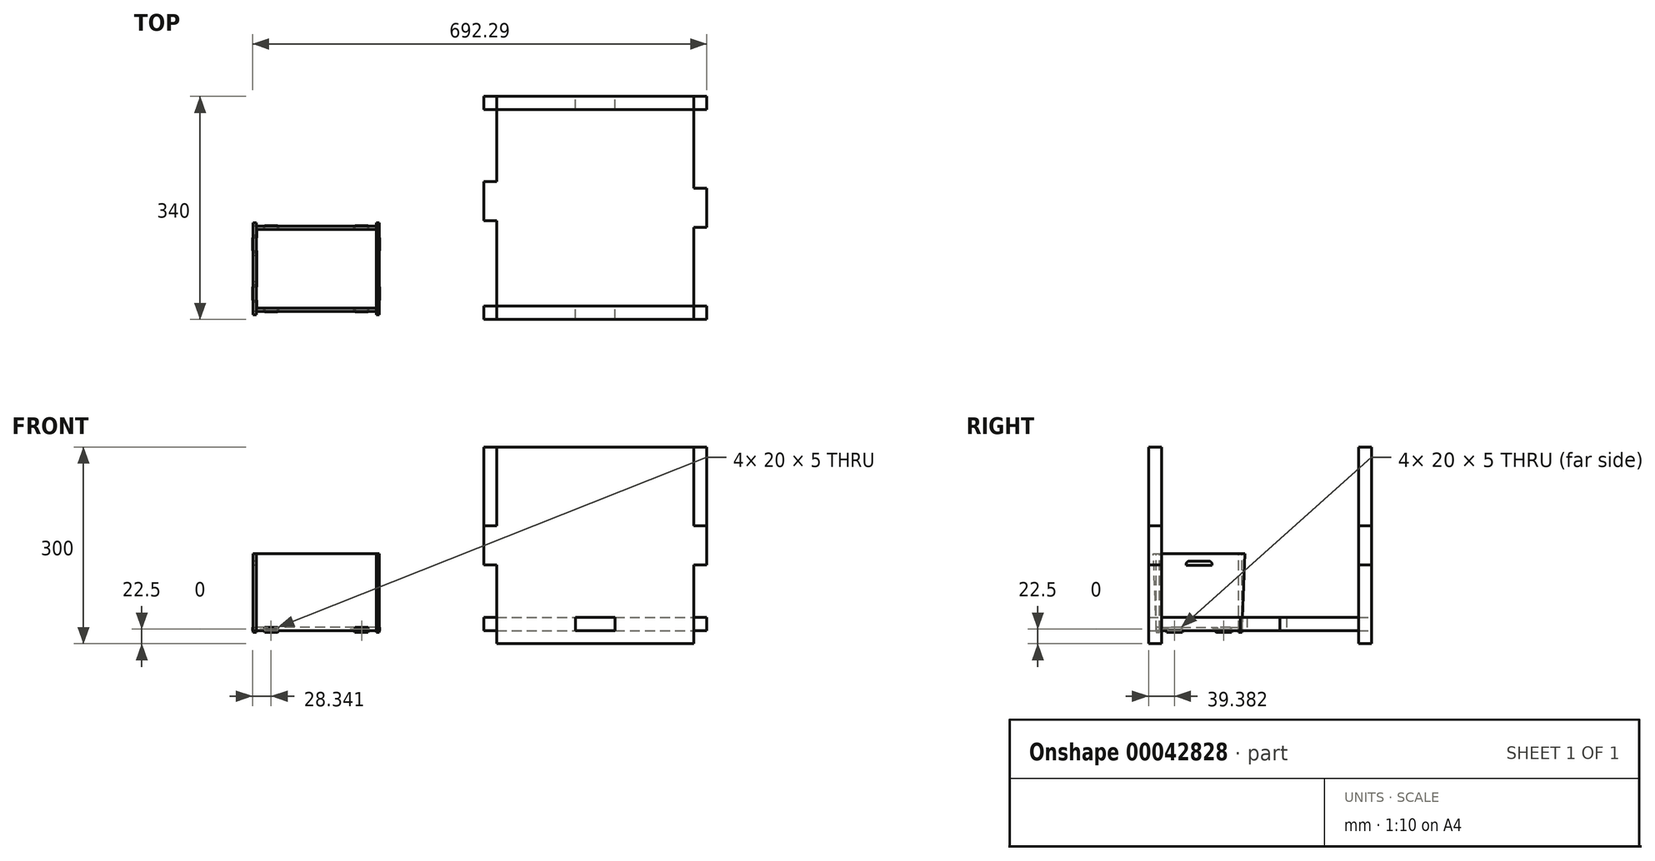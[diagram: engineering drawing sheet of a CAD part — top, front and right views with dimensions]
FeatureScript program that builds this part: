
annotation { "Feature Type Name" : "Feature", "Feature Type Description" : "" }
export const myFeature = defineFeature(function(context is Context, id is Id, definition is map)
    precondition{}
    {
        {
            var Q0;
            Q0=qCreatedBy(makeId("Top.planeOp"),FACE);
            var sketch = newSketch(context, id + "F0", { "sketchPlane" : qUnion([Q0])});
            skLineSegment(sketch, "E0.rect.bottom", {"start": v(91.08, -60.14) * mm, "end": v(-91.08, -60.14) * mm});
            skLineSegment(sketch, "E0.rect.top", {"start": v(91.08, 60.14) * mm, "end": v(-91.08, 60.14) * mm});
            skLineSegment(sketch, "E0.rect.left", {"start": v(91.08, -60.14) * mm, "end": v(91.08, 60.14) * mm});
            skLineSegment(sketch, "E0.rect.right", {"start": v(-91.08, -60.14) * mm, "end": v(-91.08, 60.14) * mm});
            skPoint(sketch, "E0.rect.middle", {"position": v(0, 0) * mm});
            skLineSegment(sketch, "E1.rect.bottom", {"start": v(78.98, 54.64) * mm, "end": v(58.98, 54.64) * mm});
            skLineSegment(sketch, "E1.rect.top", {"start": v(78.98, 65.64) * mm, "end": v(58.98, 65.64) * mm});
            skLineSegment(sketch, "E1.rect.left", {"start": v(78.98, 54.64) * mm, "end": v(78.98, 65.64) * mm});
            skLineSegment(sketch, "E1.rect.right", {"start": v(58.98, 54.64) * mm, "end": v(58.98, 65.64) * mm});
            skPoint(sketch, "E1.rect.middle", {"position": v(68.98, 60.14) * mm});
            skLineSegment(sketch, "E2.rect.bottom", {"start": v(58.98, -54.64) * mm, "end": v(78.98, -54.64) * mm});
            skLineSegment(sketch, "E2.rect.top", {"start": v(58.98, -65.64) * mm, "end": v(78.98, -65.64) * mm});
            skLineSegment(sketch, "E2.rect.left", {"start": v(58.98, -54.64) * mm, "end": v(58.98, -65.64) * mm});
            skLineSegment(sketch, "E2.rect.right", {"start": v(78.98, -54.64) * mm, "end": v(78.98, -65.64) * mm});
            skPoint(sketch, "E2.rect.middle", {"position": v(68.98, -60.14) * mm});
            skLineSegment(sketch, "E3.rect.bottom", {"start": v(96.58, 27.63) * mm, "end": v(85.58, 27.63) * mm});
            skLineSegment(sketch, "E3.rect.top", {"start": v(96.58, 47.63) * mm, "end": v(85.58, 47.63) * mm});
            skLineSegment(sketch, "E3.rect.left", {"start": v(96.58, 27.63) * mm, "end": v(96.58, 47.63) * mm});
            skLineSegment(sketch, "E3.rect.right", {"start": v(85.58, 27.63) * mm, "end": v(85.58, 47.63) * mm});
            skPoint(sketch, "E3.rect.middle", {"position": v(91.08, 37.63) * mm});
            skLineSegment(sketch, "E4.rect.bottom", {"start": v(-97.32, 47.63) * mm, "end": v(-86.32, 47.63) * mm});
            skLineSegment(sketch, "E4.rect.top", {"start": v(-97.32, 27.63) * mm, "end": v(-86.32, 27.63) * mm});
            skLineSegment(sketch, "E4.rect.left", {"start": v(-97.32, 47.63) * mm, "end": v(-97.32, 27.63) * mm});
            skLineSegment(sketch, "E4.rect.right", {"start": v(-86.32, 47.63) * mm, "end": v(-86.32, 27.63) * mm});
            skLineSegment(sketch, "E5", {"start": v(0, -60.14) * mm, "end": v(0, -76.16) * mm, "construction": true});
            skLineSegment(sketch, "E6.MirrorCS", {"start": v(-58.98, -65.64) * mm, "end": v(-78.98, -65.64) * mm});
            skLineSegment(sketch, "E7.MirrorCS", {"start": v(-58.98, -54.64) * mm, "end": v(-58.98, -65.64) * mm});
            skLineSegment(sketch, "E8.MirrorCS", {"start": v(-78.98, -54.64) * mm, "end": v(-78.98, -65.64) * mm});
            skPoint(sketch, "E9", {"position": v(-91.08, 0) * mm});
            skLineSegment(sketch, "E10", {"start": v(-91.08, 0) * mm, "end": v(-66.47, 0) * mm, "construction": true});
            skLineSegment(sketch, "E11.MirrorCS", {"start": v(-97.32, -27.63) * mm, "end": v(-86.32, -27.63) * mm});
            skLineSegment(sketch, "E12.MirrorCS", {"start": v(-97.32, -47.63) * mm, "end": v(-97.32, -27.63) * mm});
            skLineSegment(sketch, "E13.MirrorCS", {"start": v(-97.32, -47.63) * mm, "end": v(-86.32, -47.63) * mm});
            skLineSegment(sketch, "E14.MirrorCS", {"start": v(96.58, -27.63) * mm, "end": v(85.58, -27.63) * mm});
            skLineSegment(sketch, "E15.MirrorCS", {"start": v(96.58, -27.63) * mm, "end": v(96.58, -47.63) * mm});
            skLineSegment(sketch, "E16.MirrorCS", {"start": v(96.58, -47.63) * mm, "end": v(85.58, -47.63) * mm});
            skLineSegment(sketch, "E17.bottom", {"start": v(-78.98, 53.09) * mm, "end": v(-58.98, 53.09) * mm});
            skLineSegment(sketch, "E17.top", {"start": v(-78.98, 65.64) * mm, "end": v(-58.98, 65.64) * mm});
            skLineSegment(sketch, "E17.left", {"start": v(-78.98, 53.09) * mm, "end": v(-78.98, 65.64) * mm});
            skLineSegment(sketch, "E17.right", {"start": v(-58.98, 53.09) * mm, "end": v(-58.98, 65.64) * mm});
            skSolve(sketch);
        }
        {
            var Q0;
            Q0 = qSketchRegion(id + "F0", true);
            extrude(context, id + "F1", {"entities" : qUnion([Q0]), "depth" : 5 * mm});
        }
        {
            var Q0;
            {var subQ0=sQuery(id+"F0.wireOp",EDGE,"E0.rect.left");Q0=makeQuery(id+"F1.opExtrude","SWEPT_FACE",FACE,{"disambiguationData":[OSD([subQ0]),TDD([makeQuery(id+"F0.imprint","IMPRINT",EDGE,{"disambiguationData":[TD([[makeQuery(id+"F0.imprint","INTERSECT",VERTEX,{"derivedFrom":[sQuery(id+"F0.wireOp",EDGE,"E0.rect.bottom"),subQ0]}),-1.0]])],"derivedFrom":subQ0})])]});}
            var sketch = newSketch(context, id + "F2", { "sketchPlane" : qUnion([Q0])});
            skLineSegment(sketch, "E18.bottom", {"start": v(-65, -2.63) * mm, "end": v(-25.7, -2.63) * mm});
            skLineSegment(sketch, "E18.top", {"start": v(-65, 117.37) * mm, "end": v(65, 117.37) * mm});
            skLineSegment(sketch, "E18.left", {"start": v(-65, -2.63) * mm, "end": v(-65, 117.37) * mm});
            skLineSegment(sketch, "E18.right", {"start": v(65, -2.63) * mm, "end": v(65, 117.37) * mm});
            skLineSegment(sketch, "E19", {"start": v(-65, -2.63) * mm, "end": v(-70, 117.37) * mm});
            skLineSegment(sketch, "E20", {"start": v(-70, 117.37) * mm, "end": v(-65, 117.37) * mm});
            skLineSegment(sketch, "E21", {"start": v(65, 117.37) * mm, "end": v(70, 117.37) * mm});
            skLineSegment(sketch, "E22", {"start": v(70, 117.37) * mm, "end": v(65, -2.63) * mm});
            skPoint(sketch, "E23", {"position": v(0, -2.63) * mm});
            skLineSegment(sketch, "E24", {"start": v(-50.88, 0) * mm, "end": v(-65.1, 0) * mm});
            skLineSegment(sketch, "E25", {"start": v(0, -2.63) * mm, "end": v(0, -7.24) * mm, "construction": true});
            skLineSegment(sketch, "E26.MirrorCS", {"start": v(50.88, 0) * mm, "end": v(65.1, 0) * mm});
            skLineSegment(sketch, "E27", {"start": v(-50.88, 0) * mm, "end": v(-49.45, -2.63) * mm});
            skLineSegment(sketch, "E28", {"start": v(-24.16, 0) * mm, "end": v(-25.7, -2.63) * mm});
            skLineSegment(sketch, "E29.MirrorCS", {"start": v(24.16, 0) * mm, "end": v(25.7, -2.63) * mm});
            skLineSegment(sketch, "E30.MirrorCS", {"start": v(50.88, 0) * mm, "end": v(49.45, -2.63) * mm});
            skLineSegment(sketch, "E31.trimOffspring", {"start": v(25.7, -2.63) * mm, "end": v(65, -2.63) * mm});
            skLineSegment(sketch, "E32", {"start": v(-24.16, 0) * mm, "end": v(24.16, 0) * mm});
            skSolve(sketch);
        }
        {
            var Q0;
            {var subQ0=sQuery(id+"F0.wireOp",EDGE,"E0.rect.left");var subQ1=sQuery(id+"F0.wireOp",EDGE,"E3.rect.bottom");Q0=makeQuery(id+"F2.imprint","IMPRINT",FACE,{"disambiguationData":[TD([[makeQuery(id+"F2.imprint","IMPRINT",EDGE,{"derivedFrom":makeQuery(id+"F1.opExtrude","SWEPT_EDGE",EDGE,{"disambiguationData":[OSD([subQ0,subQ1])]})}),-1.0]])]});}
            var Q1;
            {var subQ1=sQuery(id+"F0.wireOp",EDGE,"E0.rect.left");var subQ3=sQuery(id+"F0.wireOp",EDGE,"E0.rect.bottom");var subQ7=makeQuery(id+"F1.opExtrude","SWEPT_EDGE",EDGE,{"disambiguationData":[OSD([subQ3,subQ1])]});Q1=makeQuery(id+"F2.imprint","IMPRINT",FACE,{"disambiguationData":[TD([[makeQuery(id+"F2.imprint","IMPRINT",EDGE,{"derivedFrom":subQ7}),1.0]])]});}
            var Q2;
            {var subQ8=sQuery(id+"F2.wireOp",EDGE,"E18.top");Q2=makeQuery(id+"F2.imprint","IMPRINT",FACE,{"disambiguationData":[TD([[makeQuery(id+"F2.imprint","IMPRINT",EDGE,{"derivedFrom":subQ8}),-1.0]])]});}
            var Q3;
            {var subQ0=sQuery(id+"F2.wireOp",EDGE,"E20");Q3=makeQuery(id+"F2.imprint","IMPRINT",FACE,{"disambiguationData":[TD([[makeQuery(id+"F2.imprint","IMPRINT",EDGE,{"derivedFrom":subQ0}),-1.0]])]});}
            var Q4;
            {var subQ5=sQuery(id+"F2.wireOp",EDGE,"E21");Q4=makeQuery(id+"F2.imprint","IMPRINT",FACE,{"disambiguationData":[TD([[makeQuery(id+"F2.imprint","IMPRINT",EDGE,{"derivedFrom":subQ5}),-1.0]])]});}
            extrude(context, id + "F3", {"entities" : qUnion([Q0, Q1, Q2, Q3, Q4]), "depth" : 5 * mm});
        }
        {
            var Q0;
            Q0=makeQuery(id+"F3.opExtrude","SWEPT_BODY",BODY,{"disambiguationData":[OSD([sQuery(id+"F2.wireOp",EDGE,"E18.bottom"),sQuery(id+"F2.wireOp",EDGE,"E18.top"),sQuery(id+"F2.wireOp",EDGE,"E19"),sQuery(id+"F2.wireOp",EDGE,"E20"),sQuery(id+"F2.wireOp",EDGE,"E21"),sQuery(id+"F2.wireOp",EDGE,"E22")])]});
            var Q1;
            {var subQ0=sQuery(id+"F0.wireOp",EDGE,"E0.rect.bottom");Q1=makeQuery(id+"F1.opExtrude","CAP_EDGE",EDGE,{"disambiguationData":[OSD([subQ0]),TDD([makeQuery(id+"F0.imprint","IMPRINT",EDGE,{"disambiguationData":[TD([[makeQuery(id+"F0.imprint","INTERSECT",VERTEX,{"derivedFrom":[subQ0,sQuery(id+"F0.wireOp",EDGE,"E7.MirrorCS")]}),1.0]])],"derivedFrom":subQ0})])],"isStart":false});}
            transform(context, id + "F4", {"entities" : qUnion([Q0]), "transformType" : TransformType.TRANSLATION_DISTANCE, "transformDirection" : qUnion([Q1]), "distance" : 187.5 * mm, "makeCopy" : true});
        }
        {
            var Q0;
            {var subQ0=sQuery(id+"F0.wireOp",EDGE,"E0.rect.bottom");Q0=makeQuery(id+"F1.opExtrude","SWEPT_FACE",FACE,{"disambiguationData":[OSD([subQ0]),TDD([makeQuery(id+"F0.imprint","IMPRINT",EDGE,{"disambiguationData":[TD([[makeQuery(id+"F0.imprint","INTERSECT",VERTEX,{"derivedFrom":[subQ0,sQuery(id+"F0.wireOp",EDGE,"E0.rect.right")]}),1.0]])],"derivedFrom":subQ0})])]});}
            var sketch = newSketch(context, id + "F5", { "sketchPlane" : qUnion([Q0])});
            skLineSegment(sketch, "E33.bottom", {"start": v(-91.42, -2.63) * mm, "end": v(91.08, -2.63) * mm});
            skLineSegment(sketch, "E33.top", {"start": v(-91.42, 117.37) * mm, "end": v(91.08, 117.37) * mm});
            skLineSegment(sketch, "E33.left", {"start": v(-91.42, -2.63) * mm, "end": v(-91.42, 117.37) * mm});
            skLineSegment(sketch, "E33.right", {"start": v(91.08, -2.63) * mm, "end": v(91.08, 117.37) * mm});
            skLineSegment(sketch, "E34", {"start": v(-91.42, 0) * mm, "end": v(-80.28, 0) * mm});
            skLineSegment(sketch, "E35", {"start": v(-80.28, 0) * mm, "end": v(-79.07, -2.63) * mm});
            skLineSegment(sketch, "E36", {"start": v(-57.5, 0) * mm, "end": v(-58.88, -2.63) * mm});
            skLineSegment(sketch, "E37", {"start": v(-0.17, -5.62) * mm, "end": v(-0.17, -18.88) * mm, "construction": true});
            skPoint(sketch, "E37.startSnap0", {"position": v(-0.17, -2.63) * mm});
            skLineSegment(sketch, "E38.MirrorCS", {"start": v(57.17, 0) * mm, "end": v(58.54, -2.63) * mm});
            skLineSegment(sketch, "E39.MirrorCS", {"start": v(79.94, 0) * mm, "end": v(78.74, -2.63) * mm});
            skLineSegment(sketch, "E40.MirrorCS", {"start": v(91.08, 0) * mm, "end": v(79.94, 0) * mm});
            skLineSegment(sketch, "E41", {"start": v(-57.5, 0) * mm, "end": v(57.17, 0) * mm});
            skSolve(sketch);
        }
        {
            var Q0;
            {var subQ3=sQuery(id+"F5.wireOp",EDGE,"E33.bottom");Q0=makeQuery(id+"F5.imprint","IMPRINT",FACE,{"disambiguationData":[TD([[makeQuery(id+"F5.imprint","IMPRINT",EDGE,{"derivedFrom":subQ3}),1.0]])]});}
            var Q1;
            {var subQ0=sQuery(id+"F0.wireOp",EDGE,"E0.rect.bottom");var subQ2=sQuery(id+"F0.wireOp",EDGE,"E0.rect.right");Q1=makeQuery(id+"F5.imprint","IMPRINT",FACE,{"disambiguationData":[TD([[makeQuery(id+"F5.imprint","IMPRINT",EDGE,{"derivedFrom":makeQuery(id+"F1.opExtrude","SWEPT_EDGE",EDGE,{"disambiguationData":[OSD([subQ0,subQ2])]})}),1.0]])]});}
            extrude(context, id + "F6", {"entities" : qUnion([Q0, Q1]), "depth" : 5 * mm});
        }
        {
            var Q0;
            Q0=makeQuery(id+"F6.opExtrude","SWEPT_BODY",BODY,{"disambiguationData":[OSD([sQuery(id+"F5.wireOp",EDGE,"E33.bottom"),sQuery(id+"F5.wireOp",EDGE,"E33.top"),sQuery(id+"F5.wireOp",EDGE,"E33.left"),sQuery(id+"F5.wireOp",EDGE,"E33.right"),sQuery(id+"F5.wireOp",EDGE,"E34"),sQuery(id+"F5.wireOp",EDGE,"E35"),sQuery(id+"F5.wireOp",EDGE,"E36"),sQuery(id+"F5.wireOp",EDGE,"E38.MirrorCS"),sQuery(id+"F5.wireOp",EDGE,"E39.MirrorCS"),sQuery(id+"F5.wireOp",EDGE,"E40.MirrorCS"),sQuery(id+"F5.wireOp",EDGE,"E41")])]});
            var Q1;
            {var subQ0=sQuery(id+"F0.wireOp",EDGE,"E0.rect.left");Q1=makeQuery(id+"F1.opExtrude","CAP_EDGE",EDGE,{"disambiguationData":[OSD([subQ0]),TDD([makeQuery(id+"F0.imprint","IMPRINT",EDGE,{"disambiguationData":[TD([[makeQuery(id+"F0.imprint","INTERSECT",VERTEX,{"derivedFrom":[sQuery(id+"F0.wireOp",EDGE,"E0.rect.bottom"),subQ0]}),-1.0]])],"derivedFrom":subQ0})])],"isStart":false});}
            var Q2;
            Q2=makeQuery(id+"F1.opExtrude","CAP_EDGE",EDGE,{"disambiguationData":[OSD([sQuery(id+"F0.wireOp",EDGE,"E3.rect.left")])],"isStart":false});
            var Q3;
            Q3=makeQuery(id+"F4.opPattern","COPY",EDGE,{"derivedFrom":makeQuery(id+"F3.opExtrude","CAP_EDGE",EDGE,{"disambiguationData":[OSD([sQuery(id+"F2.wireOp",EDGE,"E18.top")])],"isStart":false}),"instanceName":"1"});
            transform(context, id + "F7", {"entities" : qUnion([Q0]), "transformType" : TransformType.TRANSLATION_DISTANCE, "transformDirection" : qUnion([Q3]), "distance" : 125.5 * mm, "makeCopy" : true});
        }
        {
            var Q0;
            Q0=makeQuery(id+"F1.opExtrude","SWEPT_BODY",BODY,{"disambiguationData":[OSD([sQuery(id+"F0.wireOp",EDGE,"E0.rect.bottom"),sQuery(id+"F0.wireOp",EDGE,"E0.rect.top"),sQuery(id+"F0.wireOp",EDGE,"E0.rect.left"),sQuery(id+"F0.wireOp",EDGE,"E0.rect.right"),sQuery(id+"F0.wireOp",EDGE,"E1.rect.top"),sQuery(id+"F0.wireOp",EDGE,"E1.rect.left"),sQuery(id+"F0.wireOp",EDGE,"E1.rect.right"),sQuery(id+"F0.wireOp",EDGE,"E2.rect.top"),sQuery(id+"F0.wireOp",EDGE,"E2.rect.left"),sQuery(id+"F0.wireOp",EDGE,"E2.rect.right"),sQuery(id+"F0.wireOp",EDGE,"E3.rect.bottom"),sQuery(id+"F0.wireOp",EDGE,"E3.rect.top"),sQuery(id+"F0.wireOp",EDGE,"E3.rect.left"),sQuery(id+"F0.wireOp",EDGE,"E4.rect.bottom"),sQuery(id+"F0.wireOp",EDGE,"E4.rect.top"),sQuery(id+"F0.wireOp",EDGE,"E4.rect.left")])]});
            var Q1;
            Q1=makeQuery(id+"F7.opPattern","COPY",BODY,{"derivedFrom":makeQuery(id+"F6.opExtrude","SWEPT_BODY",BODY,{"disambiguationData":[OSD([sQuery(id+"F5.wireOp",EDGE,"46b3cb84-1207-44b6-bca0-a6f87da00f9c.bottom"),sQuery(id+"F5.wireOp",EDGE,"46b3cb84-1207-44b6-bca0-a6f87da00f9c.top"),sQuery(id+"F5.wireOp",EDGE,"46b3cb84-1207-44b6-bca0-a6f87da00f9c.left"),sQuery(id+"F5.wireOp",EDGE,"46b3cb84-1207-44b6-bca0-a6f87da00f9c.right"),sQuery(id+"F5.wireOp",EDGE,"da92aac8-b902-4d4c-b7ad-71e9202061bc.rect.bottom"),sQuery(id+"F5.wireOp",EDGE,"da92aac8-b902-4d4c-b7ad-71e9202061bc.rect.top"),sQuery(id+"F5.wireOp",EDGE,"da92aac8-b902-4d4c-b7ad-71e9202061bc.rect.left"),sQuery(id+"F5.wireOp",EDGE,"ea491399-d061-4eb9-b57f-cc231cf8a471.rect.bottom"),sQuery(id+"F5.wireOp",EDGE,"ea491399-d061-4eb9-b57f-cc231cf8a471.rect.top"),sQuery(id+"F5.wireOp",EDGE,"ea491399-d061-4eb9-b57f-cc231cf8a471.rect.right")])]}),"instanceName":"1"});
            var Q2;
            Q2=makeQuery(id+"F4.opPattern","COPY",BODY,{"derivedFrom":makeQuery(id+"F3.opExtrude","SWEPT_BODY",BODY,{"disambiguationData":[OSD([sQuery(id+"F2.wireOp",EDGE,"E18.bottom"),sQuery(id+"F2.wireOp",EDGE,"E18.top"),sQuery(id+"F2.wireOp",EDGE,"E19"),sQuery(id+"F2.wireOp",EDGE,"E20"),sQuery(id+"F2.wireOp",EDGE,"E21"),sQuery(id+"F2.wireOp",EDGE,"E22")])]}),"instanceName":"1"});
            var Q3;
            Q3=makeQuery(id+"F3.opExtrude","SWEPT_BODY",BODY,{"disambiguationData":[OSD([sQuery(id+"F2.wireOp",EDGE,"E18.bottom"),sQuery(id+"F2.wireOp",EDGE,"E18.top"),sQuery(id+"F2.wireOp",EDGE,"E19"),sQuery(id+"F2.wireOp",EDGE,"E20"),sQuery(id+"F2.wireOp",EDGE,"E21"),sQuery(id+"F2.wireOp",EDGE,"E22")])]});
            var Q4;
            Q4=makeQuery(id+"F6.opExtrude","SWEPT_BODY",BODY,{"disambiguationData":[OSD([sQuery(id+"F5.wireOp",EDGE,"46b3cb84-1207-44b6-bca0-a6f87da00f9c.bottom"),sQuery(id+"F5.wireOp",EDGE,"46b3cb84-1207-44b6-bca0-a6f87da00f9c.top"),sQuery(id+"F5.wireOp",EDGE,"46b3cb84-1207-44b6-bca0-a6f87da00f9c.left"),sQuery(id+"F5.wireOp",EDGE,"46b3cb84-1207-44b6-bca0-a6f87da00f9c.right"),sQuery(id+"F5.wireOp",EDGE,"da92aac8-b902-4d4c-b7ad-71e9202061bc.rect.bottom"),sQuery(id+"F5.wireOp",EDGE,"da92aac8-b902-4d4c-b7ad-71e9202061bc.rect.top"),sQuery(id+"F5.wireOp",EDGE,"da92aac8-b902-4d4c-b7ad-71e9202061bc.rect.left"),sQuery(id+"F5.wireOp",EDGE,"ea491399-d061-4eb9-b57f-cc231cf8a471.rect.bottom"),sQuery(id+"F5.wireOp",EDGE,"ea491399-d061-4eb9-b57f-cc231cf8a471.rect.top"),sQuery(id+"F5.wireOp",EDGE,"ea491399-d061-4eb9-b57f-cc231cf8a471.rect.right")])]});
            booleanBodies(context, id + "F8", {"operationType" : BooleanOperationType.SUBTRACTION, "tools" : qUnion([Q0]), "targets" : qUnion([Q1, Q2, Q3, Q4]), "keepTools" : true});
        }
        {
            var Q0;
            Q0=makeQuery(id+"F1.opExtrude","SWEPT_BODY",BODY,{"disambiguationData":[OSD([sQuery(id+"F0.wireOp",EDGE,"E0.rect.bottom"),sQuery(id+"F0.wireOp",EDGE,"E0.rect.top"),sQuery(id+"F0.wireOp",EDGE,"E0.rect.left"),sQuery(id+"F0.wireOp",EDGE,"E0.rect.right"),sQuery(id+"F0.wireOp",EDGE,"E1.rect.top"),sQuery(id+"F0.wireOp",EDGE,"E1.rect.left"),sQuery(id+"F0.wireOp",EDGE,"E1.rect.right"),sQuery(id+"F0.wireOp",EDGE,"E2.rect.top"),sQuery(id+"F0.wireOp",EDGE,"E2.rect.left"),sQuery(id+"F0.wireOp",EDGE,"E2.rect.right"),sQuery(id+"F0.wireOp",EDGE,"E3.rect.bottom"),sQuery(id+"F0.wireOp",EDGE,"E3.rect.top"),sQuery(id+"F0.wireOp",EDGE,"E3.rect.left"),sQuery(id+"F0.wireOp",EDGE,"E4.rect.bottom"),sQuery(id+"F0.wireOp",EDGE,"E4.rect.top"),sQuery(id+"F0.wireOp",EDGE,"E4.rect.left"),sQuery(id+"F0.wireOp",EDGE,"E6.MirrorCS"),sQuery(id+"F0.wireOp",EDGE,"E7.MirrorCS"),sQuery(id+"F0.wireOp",EDGE,"E8.MirrorCS"),sQuery(id+"F0.wireOp",EDGE,"E11.MirrorCS"),sQuery(id+"F0.wireOp",EDGE,"E12.MirrorCS"),sQuery(id+"F0.wireOp",EDGE,"E13.MirrorCS"),sQuery(id+"F0.wireOp",EDGE,"E14.MirrorCS"),sQuery(id+"F0.wireOp",EDGE,"E15.MirrorCS"),sQuery(id+"F0.wireOp",EDGE,"E16.MirrorCS"),sQuery(id+"F0.wireOp",EDGE,"E17.top"),sQuery(id+"F0.wireOp",EDGE,"E17.left"),sQuery(id+"F0.wireOp",EDGE,"E17.right")])]});
            var Q1;
            Q1=makeQuery(id+"F6.opExtrude","SWEPT_BODY",BODY,{"disambiguationData":[OSD([sQuery(id+"F5.wireOp",EDGE,"E33.bottom"),sQuery(id+"F5.wireOp",EDGE,"E33.top"),sQuery(id+"F5.wireOp",EDGE,"E33.left"),sQuery(id+"F5.wireOp",EDGE,"E33.right"),sQuery(id+"F5.wireOp",EDGE,"E34"),sQuery(id+"F5.wireOp",EDGE,"E35"),sQuery(id+"F5.wireOp",EDGE,"E36"),sQuery(id+"F5.wireOp",EDGE,"E38.MirrorCS"),sQuery(id+"F5.wireOp",EDGE,"E39.MirrorCS"),sQuery(id+"F5.wireOp",EDGE,"E40.MirrorCS"),sQuery(id+"F5.wireOp",EDGE,"E41")])]});
            var Q2;
            Q2=makeQuery(id+"F7.opPattern","COPY",BODY,{"derivedFrom":makeQuery(id+"F6.opExtrude","SWEPT_BODY",BODY,{"disambiguationData":[OSD([sQuery(id+"F5.wireOp",EDGE,"E33.bottom"),sQuery(id+"F5.wireOp",EDGE,"E33.top"),sQuery(id+"F5.wireOp",EDGE,"E33.left"),sQuery(id+"F5.wireOp",EDGE,"E33.right"),sQuery(id+"F5.wireOp",EDGE,"E34"),sQuery(id+"F5.wireOp",EDGE,"E35"),sQuery(id+"F5.wireOp",EDGE,"E36"),sQuery(id+"F5.wireOp",EDGE,"E38.MirrorCS"),sQuery(id+"F5.wireOp",EDGE,"E39.MirrorCS"),sQuery(id+"F5.wireOp",EDGE,"E40.MirrorCS"),sQuery(id+"F5.wireOp",EDGE,"E41")])]}),"instanceName":"1"});
            booleanBodies(context, id + "F9", {"operationType" : BooleanOperationType.SUBTRACTION, "tools" : qUnion([Q0]), "targets" : qUnion([Q1, Q2]), "offsetAll" : true, "keepTools" : true});
        }
        {
            var Q0;
            Q0=makeQuery(id+"F4.opPattern","COPY",FACE,{"derivedFrom":makeQuery(id+"F3.opExtrude","CAP_FACE",FACE,{"disambiguationData":[OSD([sQuery(id+"F2.wireOp",EDGE,"E18.bottom"),sQuery(id+"F2.wireOp",EDGE,"E18.top"),sQuery(id+"F2.wireOp",EDGE,"E19"),sQuery(id+"F2.wireOp",EDGE,"E20"),sQuery(id+"F2.wireOp",EDGE,"E21"),sQuery(id+"F2.wireOp",EDGE,"E22"),sQuery(id+"F2.wireOp",EDGE,"E24"),sQuery(id+"F2.wireOp",EDGE,"E26.MirrorCS"),sQuery(id+"F2.wireOp",EDGE,"E27"),sQuery(id+"F2.wireOp",EDGE,"E28"),sQuery(id+"F2.wireOp",EDGE,"E29.MirrorCS"),sQuery(id+"F2.wireOp",EDGE,"E30.MirrorCS"),sQuery(id+"F2.wireOp",EDGE,"E31.trimOffspring"),sQuery(id+"F2.wireOp",EDGE,"E32")])],"isStart":true}),"instanceName":"1"});
            var sketch = newSketch(context, id + "F10", { "sketchPlane" : qUnion([Q0])});
            skLineSegment(sketch, "E42.rect.bottom", {"start": v(19.76, 99.75) * mm, "end": v(-19.76, 99.75) * mm});
            skLineSegment(sketch, "E42.rect.top", {"start": v(19.76, 106.08) * mm, "end": v(-19.76, 106.08) * mm});
            skLineSegment(sketch, "E42.rect.left", {"start": v(19.76, 99.75) * mm, "end": v(19.76, 106.08) * mm});
            skLineSegment(sketch, "E42.rect.right", {"start": v(-19.76, 99.75) * mm, "end": v(-19.76, 106.08) * mm});
            skPoint(sketch, "E42.rect.middle", {"position": v(0, 102.92) * mm});
            skPoint(sketch, "E42.rect.middle.positionSnap0", {"position": v(0, 117.37) * mm});
            skPoint(sketch, "E42.rect.centerSnap0", {"position": v(0, 117.37) * mm});
            skSolve(sketch);
        }
        {
            var Q0;
            Q0 = qSketchRegion(id + "F10", true);
            var Q1;
            Q1=makeQuery(id+"F3.opExtrude","CAP_FACE",FACE,{"disambiguationData":[OSD([sQuery(id+"F2.wireOp",EDGE,"E18.bottom"),sQuery(id+"F2.wireOp",EDGE,"E18.top"),sQuery(id+"F2.wireOp",EDGE,"E19"),sQuery(id+"F2.wireOp",EDGE,"E20"),sQuery(id+"F2.wireOp",EDGE,"E21"),sQuery(id+"F2.wireOp",EDGE,"E22"),sQuery(id+"F2.wireOp",EDGE,"E24"),sQuery(id+"F2.wireOp",EDGE,"E26.MirrorCS"),sQuery(id+"F2.wireOp",EDGE,"E27"),sQuery(id+"F2.wireOp",EDGE,"E28"),sQuery(id+"F2.wireOp",EDGE,"E29.MirrorCS"),sQuery(id+"F2.wireOp",EDGE,"E30.MirrorCS"),sQuery(id+"F2.wireOp",EDGE,"E31.trimOffspring"),sQuery(id+"F2.wireOp",EDGE,"E32")])],"isStart":false});
            extrude(context, id + "F11", {"entities" : qUnion([Q0]), "operationType" : NewBodyOperationType.REMOVE, "endBound" : BoundingType.UP_TO_SURFACE, "oppositeDirection" : true, "endBoundEntityFace" : qUnion([Q1]), "depth" : 25 * mm});
        }
        {
            var Q0;
            Q0=makeQuery(id+"F11.boolean.opBoolean","COPY",EDGE,{"disambiguationData":[OD(0.0)],"derivedFrom":makeQuery(id+"F11.opExtrude","SWEPT_EDGE",EDGE,{"disambiguationData":[OSD([sQuery(id+"F10.wireOp",EDGE,"E42.rect.top"),sQuery(id+"F10.wireOp",EDGE,"E42.rect.right")])]})});
            var Q1;
            Q1=makeQuery(id+"F11.boolean.opBoolean","COPY",EDGE,{"disambiguationData":[OD(0.0)],"derivedFrom":makeQuery(id+"F11.opExtrude","SWEPT_EDGE",EDGE,{"disambiguationData":[OSD([sQuery(id+"F10.wireOp",EDGE,"E42.rect.top"),sQuery(id+"F10.wireOp",EDGE,"E42.rect.left")])]})});
            var Q2;
            Q2=makeQuery(id+"F11.boolean.opBoolean","COPY",EDGE,{"disambiguationData":[OD(1.0)],"derivedFrom":makeQuery(id+"F11.opExtrude","SWEPT_EDGE",EDGE,{"disambiguationData":[OSD([sQuery(id+"F10.wireOp",EDGE,"E42.rect.top"),sQuery(id+"F10.wireOp",EDGE,"E42.rect.left")])]})});
            var Q3;
            Q3=makeQuery(id+"F11.boolean.opBoolean","COPY",EDGE,{"disambiguationData":[OD(1.0)],"derivedFrom":makeQuery(id+"F11.opExtrude","SWEPT_EDGE",EDGE,{"disambiguationData":[OSD([sQuery(id+"F10.wireOp",EDGE,"E42.rect.top"),sQuery(id+"F10.wireOp",EDGE,"E42.rect.right")])]})});
            fillet(context, id + "F12", {"entities" : qUnion([Q0, Q1, Q2, Q3]), "radius" : 5 * mm, "tangentPropagation" : true, "allowEdgeOverflow" : false});
        }
        {
            var Q0;
            Q0=qCreatedBy(makeId("Top.planeOp"),FACE);
            var sketch = newSketch(context, id + "F13", { "sketchPlane" : qUnion([Q0])});
            skLineSegment(sketch, "E43.bottom", {"start": v(274.97, 242.99) * mm, "end": v(574.97, 242.99) * mm});
            skLineSegment(sketch, "E43.top", {"start": v(274.97, -57.01) * mm, "end": v(574.97, -57.01) * mm});
            skLineSegment(sketch, "E43.left", {"start": v(274.97, 242.99) * mm, "end": v(274.97, -57.01) * mm});
            skLineSegment(sketch, "E43.right", {"start": v(574.97, 242.99) * mm, "end": v(574.97, -57.01) * mm});
            skLineSegment(sketch, "E44.rect.bottom", {"start": v(454.97, -77.01) * mm, "end": v(394.97, -77.01) * mm});
            skLineSegment(sketch, "E44.rect.top", {"start": v(454.97, -37.01) * mm, "end": v(394.97, -37.01) * mm});
            skLineSegment(sketch, "E44.rect.left", {"start": v(454.97, -77.01) * mm, "end": v(454.97, -37.01) * mm});
            skLineSegment(sketch, "E44.rect.right", {"start": v(394.97, -77.01) * mm, "end": v(394.97, -37.01) * mm});
            skPoint(sketch, "E44.rect.middle", {"position": v(424.97, -57.01) * mm});
            skLineSegment(sketch, "E45.rect.bottom", {"start": v(294.97, 73.3) * mm, "end": v(254.97, 73.3) * mm});
            skLineSegment(sketch, "E45.rect.top", {"start": v(294.97, 133.3) * mm, "end": v(254.97, 133.3) * mm});
            skLineSegment(sketch, "E45.rect.left", {"start": v(294.97, 73.3) * mm, "end": v(294.97, 133.3) * mm});
            skLineSegment(sketch, "E45.rect.right", {"start": v(254.97, 73.3) * mm, "end": v(254.97, 133.3) * mm});
            skPoint(sketch, "E45.rect.middle", {"position": v(274.97, 103.3) * mm});
            skLineSegment(sketch, "E46.rect.bottom", {"start": v(454.97, 222.99) * mm, "end": v(394.97, 222.99) * mm});
            skLineSegment(sketch, "E46.rect.top", {"start": v(454.97, 262.99) * mm, "end": v(394.97, 262.99) * mm});
            skLineSegment(sketch, "E46.rect.left", {"start": v(454.97, 222.99) * mm, "end": v(454.97, 262.99) * mm});
            skLineSegment(sketch, "E46.rect.right", {"start": v(394.97, 222.99) * mm, "end": v(394.97, 262.99) * mm});
            skPoint(sketch, "E46.rect.middle", {"position": v(424.97, 242.99) * mm});
            skLineSegment(sketch, "E47.rect.bottom", {"start": v(594.97, 62.99) * mm, "end": v(554.97, 62.99) * mm});
            skLineSegment(sketch, "E47.rect.top", {"start": v(594.97, 122.99) * mm, "end": v(554.97, 122.99) * mm});
            skLineSegment(sketch, "E47.rect.left", {"start": v(594.97, 62.99) * mm, "end": v(594.97, 122.99) * mm});
            skLineSegment(sketch, "E47.rect.right", {"start": v(554.97, 62.99) * mm, "end": v(554.97, 122.99) * mm});
            skPoint(sketch, "E47.rect.middle", {"position": v(574.97, 92.99) * mm});
            skSolve(sketch);
        }
        {
            var Q0;
            Q0=makeQuery(id+"F13.imprint","IMPRINT",FACE,{"disambiguationData":[TD([[makeQuery(id+"F13.imprint","IMPRINT",EDGE,{"derivedFrom":sQuery(id+"F13.wireOp",EDGE,"E43.bottom")}),-1.0]])]});
            var Q1;
            {var subQ3=sQuery(id+"F13.wireOp",EDGE,"E45.rect.right");Q1=makeQuery(id+"F13.imprint","IMPRINT",FACE,{"disambiguationData":[TD([[makeQuery(id+"F13.imprint","IMPRINT",EDGE,{"derivedFrom":subQ3}),-1.0]])]});}
            var Q2;
            {var subQ3=sQuery(id+"F13.wireOp",EDGE,"E46.rect.top");Q2=makeQuery(id+"F13.imprint","IMPRINT",FACE,{"disambiguationData":[TD([[makeQuery(id+"F13.imprint","IMPRINT",EDGE,{"derivedFrom":subQ3}),1.0]])]});}
            var Q3;
            {var subQ0=sQuery(id+"F13.wireOp",EDGE,"E47.rect.left");Q3=makeQuery(id+"F13.imprint","IMPRINT",FACE,{"disambiguationData":[TD([[makeQuery(id+"F13.imprint","IMPRINT",EDGE,{"derivedFrom":subQ0}),1.0]])]});}
            var Q4;
            {var subQ3=sQuery(id+"F13.wireOp",EDGE,"E44.rect.bottom");Q4=makeQuery(id+"F13.imprint","IMPRINT",FACE,{"disambiguationData":[TD([[makeQuery(id+"F13.imprint","IMPRINT",EDGE,{"derivedFrom":subQ3}),-1.0]])]});}
            var Q5;
            {var subQ3=sQuery(id+"F13.wireOp",EDGE,"E44.rect.top");Q5=makeQuery(id+"F13.imprint","IMPRINT",FACE,{"disambiguationData":[TD([[makeQuery(id+"F13.imprint","IMPRINT",EDGE,{"derivedFrom":subQ3}),1.0]])]});}
            var Q6;
            {var subQ0=sQuery(id+"F13.wireOp",EDGE,"E47.rect.right");Q6=makeQuery(id+"F13.imprint","IMPRINT",FACE,{"disambiguationData":[TD([[makeQuery(id+"F13.imprint","IMPRINT",EDGE,{"derivedFrom":subQ0}),-1.0]])]});}
            var Q7;
            {var subQ3=sQuery(id+"F13.wireOp",EDGE,"E46.rect.bottom");Q7=makeQuery(id+"F13.imprint","IMPRINT",FACE,{"disambiguationData":[TD([[makeQuery(id+"F13.imprint","IMPRINT",EDGE,{"derivedFrom":subQ3}),-1.0]])]});}
            var Q8;
            {var subQ0=sQuery(id+"F13.wireOp",EDGE,"E45.rect.left");Q8=makeQuery(id+"F13.imprint","IMPRINT",FACE,{"disambiguationData":[TD([[makeQuery(id+"F13.imprint","IMPRINT",EDGE,{"derivedFrom":subQ0}),1.0]])]});}
            extrude(context, id + "F14", {"entities" : qUnion([Q0, Q1, Q2, Q3, Q4, Q5, Q6, Q7, Q8]), "depth" : 20 * mm});
        }
        {
            var Q0;
            {var subQ0=sQuery(id+"F13.wireOp",EDGE,"E43.top");Q0=makeQuery(id+"F14.opExtrude","SWEPT_FACE",FACE,{"disambiguationData":[OSD([subQ0]),TDD([makeQuery(id+"F13.imprint","IMPRINT",EDGE,{"disambiguationData":[TD([[makeQuery(id+"F13.imprint","INTERSECT",VERTEX,{"derivedFrom":[subQ0,sQuery(id+"F13.wireOp",EDGE,"E43.left")]}),-1.0]])],"derivedFrom":subQ0})])]});}
            var sketch = newSketch(context, id + "F15", { "sketchPlane" : qUnion([Q0])});
            skLineSegment(sketch, "E48.bottom", {"start": v(274.97, -20) * mm, "end": v(574.97, -20) * mm});
            skLineSegment(sketch, "E48.top", {"start": v(274.97, 280) * mm, "end": v(574.97, 280) * mm});
            skLineSegment(sketch, "E48.left", {"start": v(274.97, -20) * mm, "end": v(274.97, 280) * mm});
            skLineSegment(sketch, "E48.right", {"start": v(574.97, -20) * mm, "end": v(574.97, 280) * mm});
            skLineSegment(sketch, "E49.rect.bottom", {"start": v(594.97, 100) * mm, "end": v(554.97, 100) * mm});
            skLineSegment(sketch, "E49.rect.top", {"start": v(594.97, 160) * mm, "end": v(554.97, 160) * mm});
            skLineSegment(sketch, "E49.rect.left", {"start": v(594.97, 100) * mm, "end": v(594.97, 160) * mm});
            skLineSegment(sketch, "E49.rect.right", {"start": v(554.97, 100) * mm, "end": v(554.97, 160) * mm});
            skPoint(sketch, "E49.rect.middle", {"position": v(574.97, 130) * mm});
            skLineSegment(sketch, "E50.rect.bottom", {"start": v(254.97, 100) * mm, "end": v(294.97, 100) * mm});
            skLineSegment(sketch, "E50.rect.top", {"start": v(254.97, 160) * mm, "end": v(294.97, 160) * mm});
            skLineSegment(sketch, "E50.rect.left", {"start": v(254.97, 100) * mm, "end": v(254.97, 160) * mm});
            skLineSegment(sketch, "E50.rect.right", {"start": v(294.97, 100) * mm, "end": v(294.97, 160) * mm});
            skPoint(sketch, "E50.rect.middle", {"position": v(274.97, 130) * mm});
            skSolve(sketch);
        }
        {
            var Q0;
            {var subQ0=sQuery(id+"F15.wireOp",EDGE,"E50.rect.left");Q0=makeQuery(id+"F15.imprint","IMPRINT",FACE,{"disambiguationData":[TD([[makeQuery(id+"F15.imprint","IMPRINT",EDGE,{"derivedFrom":subQ0}),-1.0]])]});}
            var Q1;
            {var subQ7=sQuery(id+"F15.wireOp",EDGE,"E48.top");Q1=makeQuery(id+"F15.imprint","IMPRINT",FACE,{"disambiguationData":[TD([[makeQuery(id+"F15.imprint","IMPRINT",EDGE,{"derivedFrom":subQ7}),-1.0]])]});}
            var Q2;
            {var subQ0=sQuery(id+"F15.wireOp",EDGE,"E49.rect.left");Q2=makeQuery(id+"F15.imprint","IMPRINT",FACE,{"disambiguationData":[TD([[makeQuery(id+"F15.imprint","IMPRINT",EDGE,{"derivedFrom":subQ0}),1.0]])]});}
            var Q3;
            {var subQ0=sQuery(id+"F15.wireOp",EDGE,"E49.rect.right");Q3=makeQuery(id+"F15.imprint","IMPRINT",FACE,{"disambiguationData":[TD([[makeQuery(id+"F15.imprint","IMPRINT",EDGE,{"derivedFrom":subQ0}),-1.0]])]});}
            var Q4;
            {var subQ3=sQuery(id+"F15.wireOp",EDGE,"E50.rect.right");Q4=makeQuery(id+"F15.imprint","IMPRINT",FACE,{"disambiguationData":[TD([[makeQuery(id+"F15.imprint","IMPRINT",EDGE,{"derivedFrom":subQ3}),1.0]])]});}
            var Q5;
            {var subQ0=sQuery(id+"F13.wireOp",EDGE,"E43.top");var subQ1=sQuery(id+"F13.wireOp",EDGE,"E44.rect.right");var subQ3=makeQuery(id+"F14.opExtrude","SWEPT_EDGE",EDGE,{"disambiguationData":[OSD([subQ0,subQ1])]});Q5=makeQuery(id+"F15.imprint","IMPRINT",FACE,{"disambiguationData":[TD([[makeQuery(id+"F15.imprint","IMPRINT",EDGE,{"derivedFrom":subQ3}),-1.0]])]});}
            extrude(context, id + "F16", {"entities" : qUnion([Q0, Q1, Q2, Q3, Q4, Q5]), "depth" : 20 * mm});
        }
        {
            var Q0;
            Q0=makeQuery(id+"F16.opExtrude","CAP_FACE",FACE,{"disambiguationData":[OSD([sQuery(id+"F15.wireOp",EDGE,"E48.bottom"),sQuery(id+"F15.wireOp",EDGE,"E48.top"),sQuery(id+"F15.wireOp",EDGE,"E48.left"),sQuery(id+"F15.wireOp",EDGE,"E48.right"),sQuery(id+"F15.wireOp",EDGE,"E49.rect.bottom"),sQuery(id+"F15.wireOp",EDGE,"E49.rect.top"),sQuery(id+"F15.wireOp",EDGE,"E49.rect.left"),sQuery(id+"F15.wireOp",EDGE,"E50.rect.bottom"),sQuery(id+"F15.wireOp",EDGE,"E50.rect.top"),sQuery(id+"F15.wireOp",EDGE,"E50.rect.left")])],"isStart":true});
            cPlane(context, id + "F17", {"entities" : qUnion([Q0]), "cplaneType" : CPlaneType.OFFSET, "offset" : 150 * mm, "width" : 150 * mm, "height" : 150 * mm});
        }
        {
            var Q0;
            Q0=makeQuery(id+"F16.opExtrude","SWEPT_BODY",BODY,{"disambiguationData":[OSD([sQuery(id+"F15.wireOp",EDGE,"E48.bottom"),sQuery(id+"F15.wireOp",EDGE,"E48.top"),sQuery(id+"F15.wireOp",EDGE,"E48.left"),sQuery(id+"F15.wireOp",EDGE,"E48.right"),sQuery(id+"F15.wireOp",EDGE,"E49.rect.bottom"),sQuery(id+"F15.wireOp",EDGE,"E49.rect.top"),sQuery(id+"F15.wireOp",EDGE,"E49.rect.left"),sQuery(id+"F15.wireOp",EDGE,"E50.rect.bottom"),sQuery(id+"F15.wireOp",EDGE,"E50.rect.top"),sQuery(id+"F15.wireOp",EDGE,"E50.rect.left")])]});
            var Q1;
            Q1=qCreatedBy(id+"F17.planeOp",FACE);
            mirror(context, id + "F18", {"entities" : qUnion([Q0]), "mirrorPlane" : qUnion([Q1])});
        }
        {
            var Q0;
            {var subQ0=sQuery(id+"F15.wireOp",EDGE,"E48.right");Q0=makeQuery(id+"F16.opExtrude","SWEPT_FACE",FACE,{"disambiguationData":[OSD([subQ0]),TDD([makeQuery(id+"F15.imprint","IMPRINT",EDGE,{"disambiguationData":[TD([[makeQuery(id+"F15.imprint","INTERSECT",VERTEX,{"derivedFrom":[sQuery(id+"F15.wireOp",EDGE,"E48.top"),subQ0]}),1.0]])],"derivedFrom":subQ0})])]});}
            var sketch = newSketch(context, id + "F19", { "sketchPlane" : qUnion([Q0])});
            skLineSegment(sketch, "E51.bottom", {"start": v(-97.01, 280) * mm, "end": v(282.99, 280) * mm});
            skLineSegment(sketch, "E51.top", {"start": v(-97.01, -20) * mm, "end": v(282.99, -20) * mm});
            skLineSegment(sketch, "E51.left", {"start": v(-97.01, 280) * mm, "end": v(-97.01, -20) * mm});
            skLineSegment(sketch, "E51.right", {"start": v(282.99, 280) * mm, "end": v(282.99, -20) * mm});
            skLineSegment(sketch, "E52", {"start": v(-97.01, 280) * mm, "end": v(-77.01, -20) * mm});
            skLineSegment(sketch, "E53", {"start": v(282.99, 280) * mm, "end": v(262.99, -20) * mm});
            skLineSegment(sketch, "E54", {"start": v(-97.01, -36.47) * mm, "end": v(-97.01, -59.46) * mm, "construction": true});
            skLineSegment(sketch, "E55", {"start": v(-97.01, -47.97) * mm, "end": v(282.99, -47.97) * mm, "construction": true});
            skLineSegment(sketch, "E56", {"start": v(282.99, -36.47) * mm, "end": v(282.99, -59.46) * mm, "construction": true});
            skLineSegment(sketch, "E57", {"start": v(-77.01, -36.47) * mm, "end": v(-77.01, -59.46) * mm, "construction": true});
            skLineSegment(sketch, "E58", {"start": v(262.99, -36.47) * mm, "end": v(262.99, -59.46) * mm, "construction": true});
            skSolve(sketch);
        }
        {
            var Q0;
            {var subQ0=sQuery(id+"F15.wireOp",EDGE,"E48.right");var subQ1=sQuery(id+"F15.wireOp",EDGE,"E49.rect.top");Q0=makeQuery(id+"F19.imprint","IMPRINT",FACE,{"disambiguationData":[TD([[makeQuery(id+"F19.imprint","IMPRINT",EDGE,{"derivedFrom":makeQuery(id+"F16.opExtrude","SWEPT_EDGE",EDGE,{"disambiguationData":[OSD([subQ0,subQ1])]})}),1.0]])]});}
            var Q1;
            {var subQ6=sQuery(id+"F19.wireOp",EDGE,"E52");Q1=makeQuery(id+"F19.imprint","IMPRINT",FACE,{"disambiguationData":[TD([[makeQuery(id+"F19.imprint","IMPRINT",EDGE,{"derivedFrom":subQ6}),1.0]])]});}
            extrude(context, id + "F20", {"entities" : qUnion([Q0, Q1]), "depth" : 20 * mm});
        }
        {
            var Q0;
            {var subQ0=sQuery(id+"F13.wireOp",EDGE,"E43.left");Q0=makeQuery(id+"F14.opExtrude","SWEPT_FACE",FACE,{"disambiguationData":[OSD([subQ0]),TDD([makeQuery(id+"F13.imprint","IMPRINT",EDGE,{"disambiguationData":[TD([[makeQuery(id+"F13.imprint","INTERSECT",VERTEX,{"derivedFrom":[sQuery(id+"F13.wireOp",EDGE,"E43.top"),subQ0]}),1.0]])],"derivedFrom":subQ0})])]});}
            cPlane(context, id + "F21", {"entities" : qUnion([Q0]), "cplaneType" : CPlaneType.OFFSET, "offset" : 150 * mm, "oppositeDirection" : true, "width" : 150 * mm, "height" : 150 * mm});
        }
        {
            var Q0;
            Q0=makeQuery(id+"F20.opExtrude","SWEPT_BODY",BODY,{"disambiguationData":[OSD([sQuery(id+"F19.wireOp",EDGE,"E51.bottom"),sQuery(id+"F19.wireOp",EDGE,"E51.top"),sQuery(id+"F19.wireOp",EDGE,"E52"),sQuery(id+"F19.wireOp",EDGE,"E53")])]});
            var Q1;
            Q1=qCreatedBy(id+"F21.planeOp",FACE);
            mirror(context, id + "F22", {"entities" : qUnion([Q0]), "mirrorPlane" : qUnion([Q1])});
        }
    });
